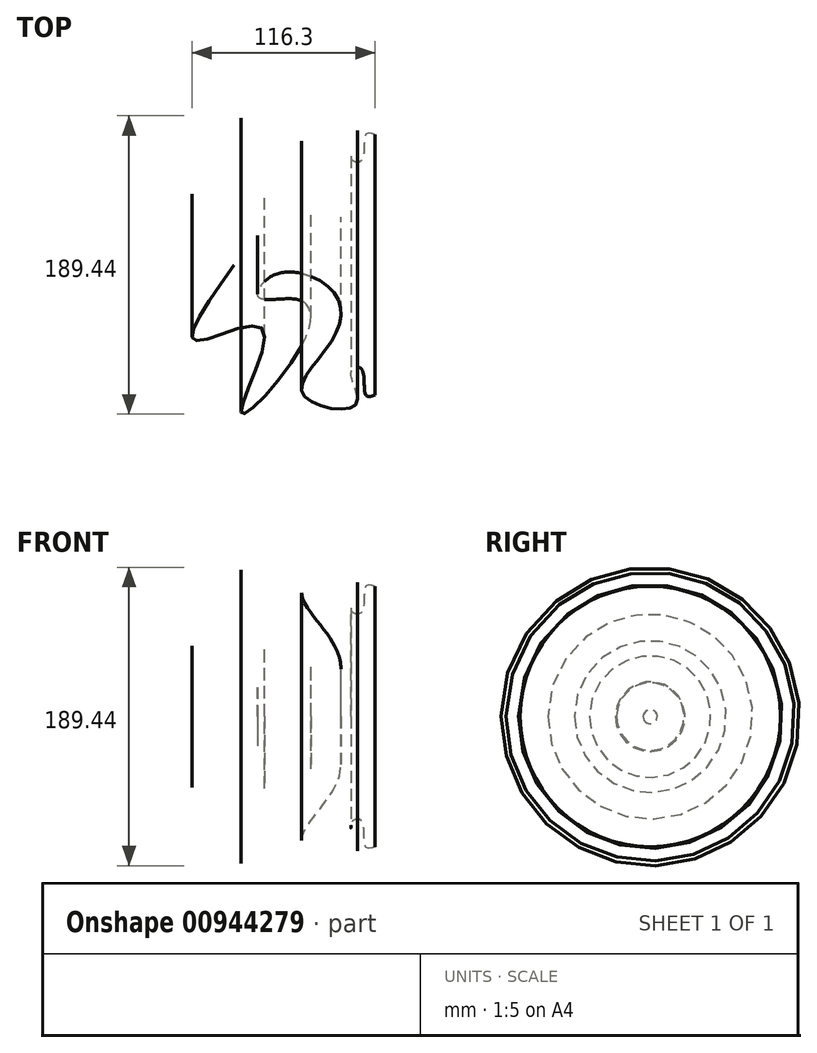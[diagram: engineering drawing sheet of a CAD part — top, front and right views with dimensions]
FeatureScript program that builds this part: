
annotation { "Feature Type Name" : "Feature", "Feature Type Description" : "" }
export const myFeature = defineFeature(function(context is Context, id is Id, definition is map)
    precondition{}
    {
        {
            var Q0;
            Q0=qCreatedBy(makeId("Top.planeOp"),FACE);
            var sketch = newSketch(context, id + "F0", { "sketchPlane" : qUnion([Q0])});
            skLineSegment(sketch, "E0", {"start": v(-38.3, 40.67) * mm, "end": v(51.38, 40.67) * mm});
            skLineSegment(sketch, "E1", {"start": v(51.38, 40.67) * mm, "end": v(51.38, -42) * mm});
            skFitSpline(sketch, "E2", {"points": [v(-38.3, 40.67) * mm, v(-62.38, -7.49) * mm, v(-20.1, 0) * mm, v(-33.75, -53.37) * mm, v(7.58, -4.83) * mm, v(2.65, 18.49) * mm, v(-22.56, 20) * mm, v(-12.13, 34.6) * mm, v(25.22, 23.04) * mm, v(23.32, -8.25) * mm, v(5.88, -42) * mm, v(39.06, -48.06) * mm, v(36.21, -27.02) * mm, v(42.66, -25.5) * mm, v(45.31, -42) * mm, v(51.38, -42) * mm], "startDerivative": vector(-547.6, -774.56) * mm, "endDerivative": vector(245.6, 87.89) * mm});
            skSolve(sketch);
        }
        {
            var Q0;
            Q0=makeQuery(id+"F0.imprint","IMPRINT",FACE,{"disambiguationData":[TD([[makeQuery(id+"F0.imprint","IMPRINT",EDGE,{"derivedFrom":sQuery(id+"F0.wireOp",EDGE,"E0")}),-1.0]])]});
            var Q1;
            Q1=sQuery(id+"F0.wireOp",EDGE,"E0");
            revolve(context, id + "F1", {"surfaceOperationType" : NewSurfaceOperationType.NEW, "entities" : qUnion([Q0]), "axis" : qUnion([Q1]), "revolveType" : RevolveType.FULL});
        }
    });
